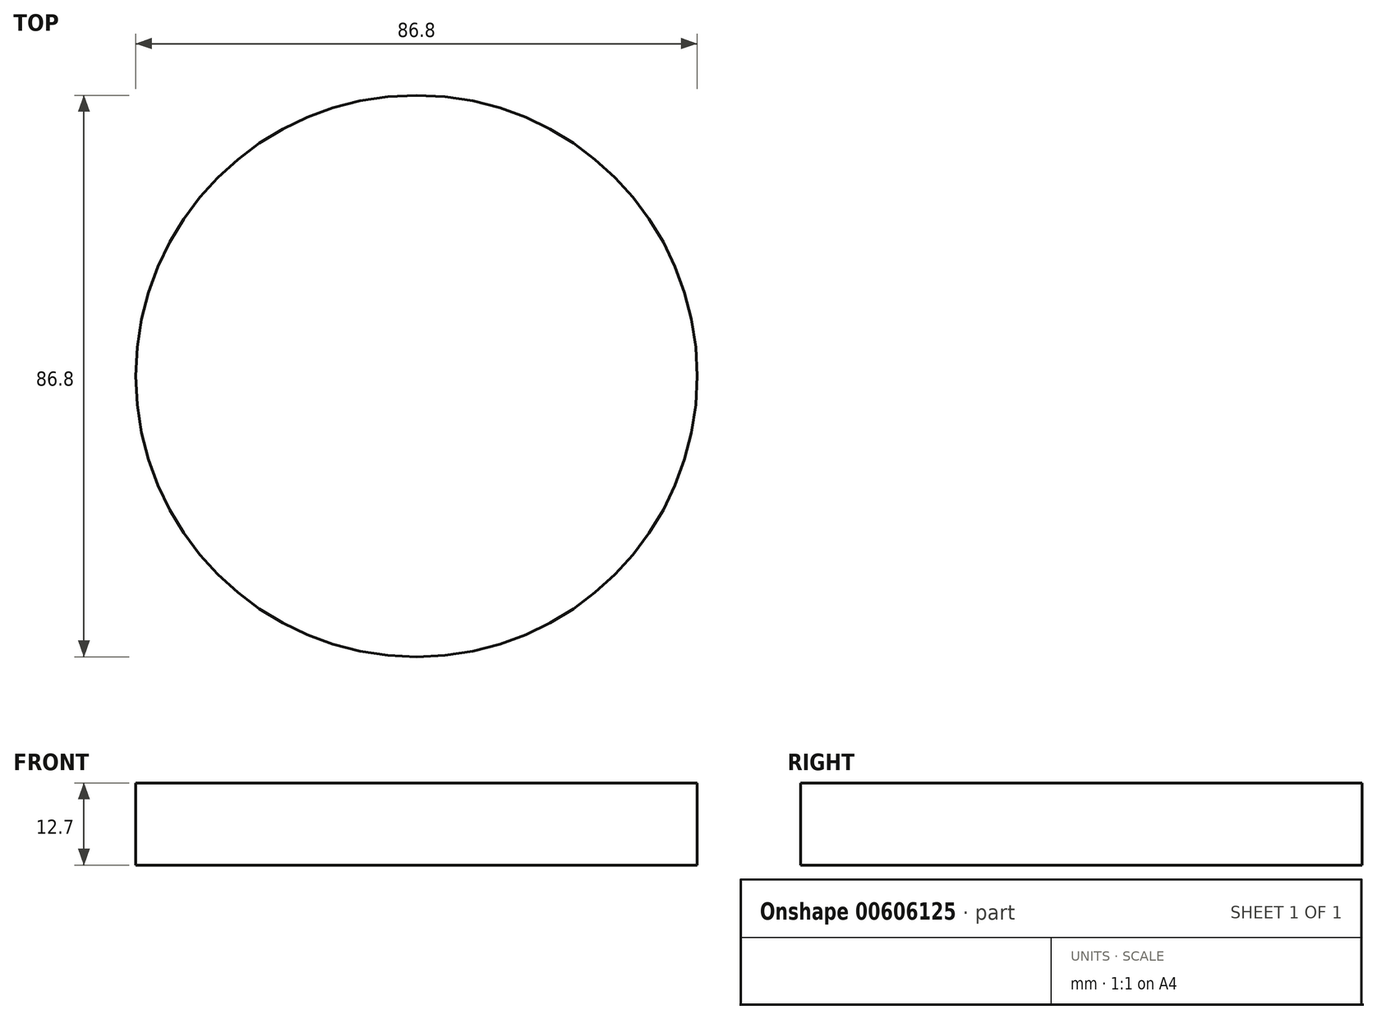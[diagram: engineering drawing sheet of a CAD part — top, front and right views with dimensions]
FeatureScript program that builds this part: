
annotation { "Feature Type Name" : "Feature", "Feature Type Description" : "" }
export const myFeature = defineFeature(function(context is Context, id is Id, definition is map)
    precondition{}
    {
        {
            var Q0;
            Q0=qCreatedBy(makeId("Top.planeOp"),FACE);
            var sketch = newSketch(context, id + "F0", { "sketchPlane" : qUnion([Q0])});
            skCircle(sketch, "E0", {"center": v(0, 0) * mm, "radius": 43.4 * mm});
            skSolve(sketch);
        }
        {
            var Q0;
            Q0=sQuery(id+"F0.wireOp",EDGE,"E0");
            extrude(context, id + "F1", {"bodyType" : ToolBodyType.SURFACE, "surfaceEntities" : qUnion([Q0]), "depth" : 12.7 * mm, "offsetDistance" : 25.4 * mm});
        }
    });
